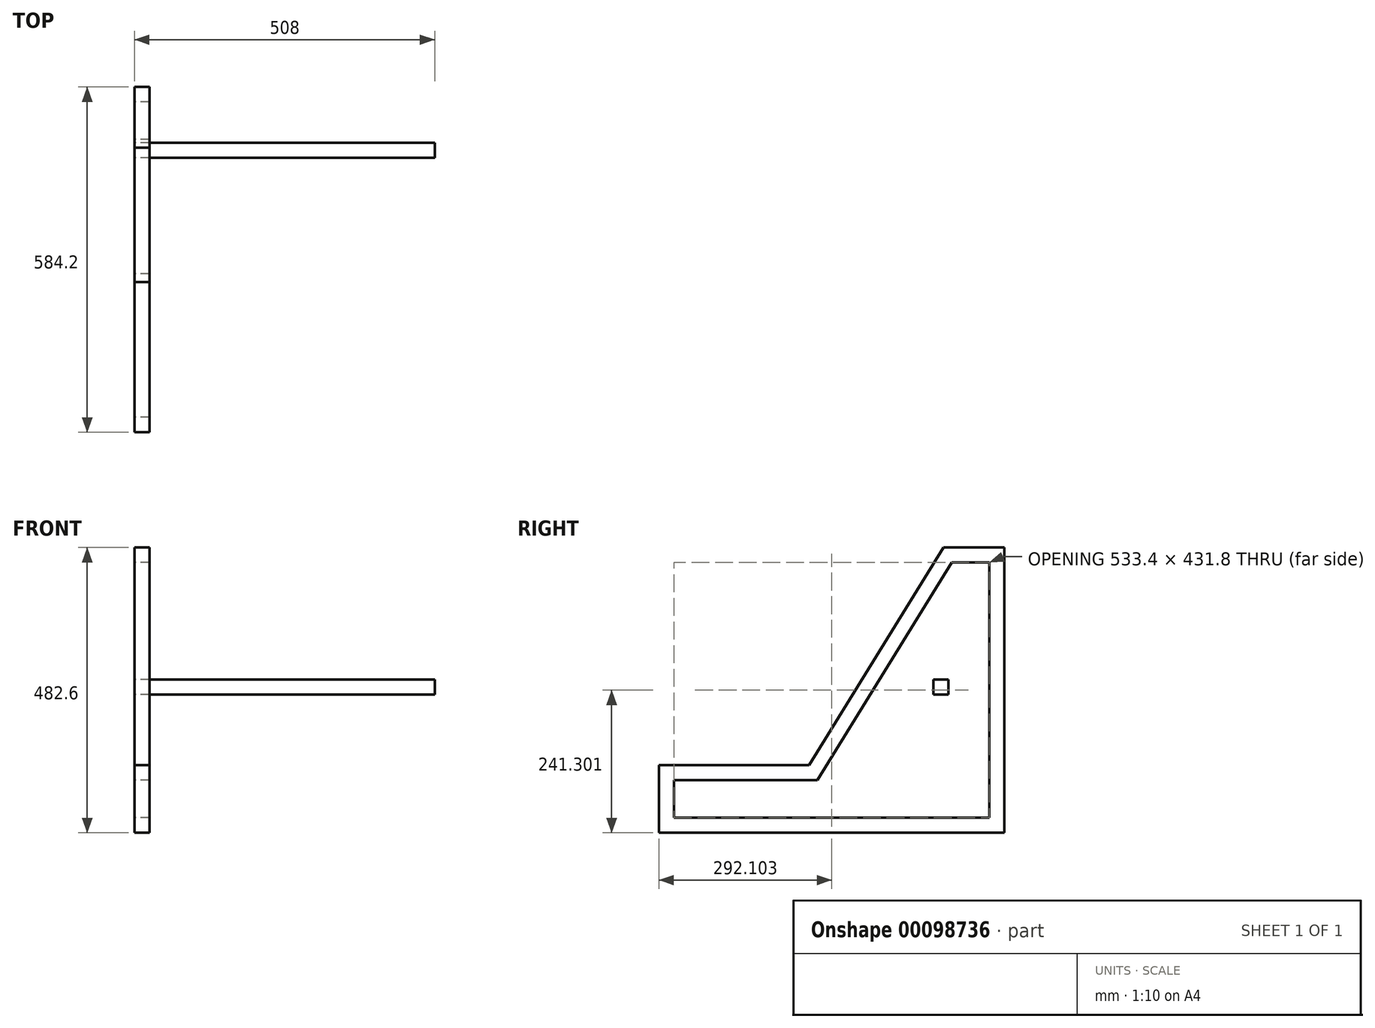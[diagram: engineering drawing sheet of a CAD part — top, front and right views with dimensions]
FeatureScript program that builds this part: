
annotation { "Feature Type Name" : "Feature", "Feature Type Description" : "" }
export const myFeature = defineFeature(function(context is Context, id is Id, definition is map)
    precondition{}
    {
        {
            var Q0;
            Q0=qCreatedBy(makeId("Right.planeOp"),FACE);
            var sketch = newSketch(context, id + "F0", { "sketchPlane" : qUnion([Q0])});
            skLineSegment(sketch, "E0", {"start": v(59.85, 261.06) * mm, "end": v(59.85, -221.54) * mm});
            skLineSegment(sketch, "E1", {"start": v(-270.35, -107.24) * mm, "end": v(-42.9, 261.06) * mm});
            skLineSegment(sketch, "E2", {"start": v(-270.35, -107.24) * mm, "end": v(-256.18, -132.64) * mm});
            skLineSegment(sketch, "E3", {"start": v(-42.9, 261.06) * mm, "end": v(-28.74, 235.66) * mm});
            skLineSegment(sketch, "E4", {"start": v(-28.74, 235.66) * mm, "end": v(-256.18, -132.64) * mm});
            skLineSegment(sketch, "E5", {"start": v(59.85, 261.06) * mm, "end": v(34.45, 235.66) * mm});
            skLineSegment(sketch, "E6", {"start": v(34.45, 235.66) * mm, "end": v(-28.74, 235.66) * mm});
            skLineSegment(sketch, "E7", {"start": v(34.45, 235.66) * mm, "end": v(34.45, -196.14) * mm});
            skLineSegment(sketch, "E8", {"start": v(59.85, 261.06) * mm, "end": v(-42.9, 261.06) * mm});
            skLineSegment(sketch, "E9", {"start": v(59.85, -221.54) * mm, "end": v(34.45, -196.14) * mm});
            skLineSegment(sketch, "E10", {"start": v(34.45, -196.14) * mm, "end": v(-498.95, -196.14) * mm});
            skLineSegment(sketch, "E11", {"start": v(59.85, -221.54) * mm, "end": v(-524.35, -221.54) * mm});
            skLineSegment(sketch, "E12", {"start": v(-524.35, -107.24) * mm, "end": v(-498.95, -132.64) * mm});
            skLineSegment(sketch, "E13", {"start": v(-524.35, -221.54) * mm, "end": v(-498.95, -196.14) * mm});
            skLineSegment(sketch, "E14", {"start": v(-256.18, -132.64) * mm, "end": v(-498.95, -132.64) * mm});
            skLineSegment(sketch, "E15", {"start": v(-498.95, -132.64) * mm, "end": v(-498.95, -196.14) * mm});
            skLineSegment(sketch, "E16", {"start": v(-524.35, -107.24) * mm, "end": v(-270.35, -107.24) * mm});
            skLineSegment(sketch, "E17", {"start": v(-524.35, -107.24) * mm, "end": v(-524.35, -221.54) * mm});
            skSolve(sketch);
        }
        {
            var Q0;
            Q0=makeQuery(id+"F0.imprint","IMPRINT",FACE,{"disambiguationData":[TD([[makeQuery(id+"F0.imprint","IMPRINT",EDGE,{"derivedFrom":sQuery(id+"F0.wireOp",EDGE,"E3")}),1.0]])]});
            var Q1;
            Q1=makeQuery(id+"F0.imprint","IMPRINT",FACE,{"disambiguationData":[TD([[makeQuery(id+"F0.imprint","IMPRINT",EDGE,{"derivedFrom":sQuery(id+"F0.wireOp",EDGE,"E1")}),-1.0]])]});
            var Q2;
            Q2=makeQuery(id+"F0.imprint","IMPRINT",FACE,{"disambiguationData":[TD([[makeQuery(id+"F0.imprint","IMPRINT",EDGE,{"derivedFrom":sQuery(id+"F0.wireOp",EDGE,"E2")}),-1.0]])]});
            var Q3;
            Q3=makeQuery(id+"F0.imprint","IMPRINT",FACE,{"disambiguationData":[TD([[makeQuery(id+"F0.imprint","IMPRINT",EDGE,{"derivedFrom":sQuery(id+"F0.wireOp",EDGE,"E12")}),-1.0]])]});
            var Q4;
            Q4=makeQuery(id+"F0.imprint","IMPRINT",FACE,{"disambiguationData":[TD([[makeQuery(id+"F0.imprint","IMPRINT",EDGE,{"derivedFrom":sQuery(id+"F0.wireOp",EDGE,"E9")}),1.0]])]});
            var Q5;
            Q5=makeQuery(id+"F0.imprint","IMPRINT",FACE,{"disambiguationData":[TD([[makeQuery(id+"F0.imprint","IMPRINT",EDGE,{"derivedFrom":sQuery(id+"F0.wireOp",EDGE,"E0")}),-1.0]])]});
            extrude(context, id + "F1", {"entities" : qUnion([Q0, Q1, Q2, Q3, Q4, Q5]), "depth" : 25.4 * mm});
        }
        {
            var Q0;
            Q0=qCreatedBy(makeId("Right.planeOp"),FACE);
            var sketch = newSketch(context, id + "F2", { "sketchPlane" : qUnion([Q0])});
            skLineSegment(sketch, "E18", {"start": v(-34.76, 38.08) * mm, "end": v(-60.16, 38.08) * mm});
            skLineSegment(sketch, "E19", {"start": v(-60.16, 38.08) * mm, "end": v(-60.16, 12.68) * mm});
            skLineSegment(sketch, "E20", {"start": v(-34.76, 38.08) * mm, "end": v(-34.76, 12.68) * mm});
            skLineSegment(sketch, "E21", {"start": v(-34.76, 12.68) * mm, "end": v(-60.16, 12.68) * mm});
            skSolve(sketch);
        }
        {
            var Q0;
            Q0=makeQuery(id+"F2.imprint","IMPRINT",FACE,{"disambiguationData":[TD([[makeQuery(id+"F2.imprint","IMPRINT",EDGE,{"derivedFrom":sQuery(id+"F2.wireOp",EDGE,"E18")}),1.0]])]});
            extrude(context, id + "F3", {"entities" : qUnion([Q0]), "depth" : 508 * mm});
        }
    });
